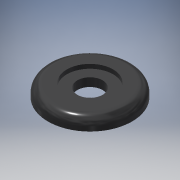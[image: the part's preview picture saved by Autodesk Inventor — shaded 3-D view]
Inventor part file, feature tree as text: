
AUTODESK INVENTOR PART (.ipt)
format: ipt  version: 2018 (Build 220112000, 112)  size: 162,816 bytes
history: native  units: mm
features: revolve x1, sketch x1
ambient origin geometry x8: Origin, YZ Plane, XZ Plane, XY Plane, X Axis, Y Axis, Z Axis, Center Point
bodies: Solid1 (feature_tree)
feature tree (2):
  revolve  "Revolution1"  [1 undecoded]
  sketch  "Sketch1"  dims[d0=5.0mm d1=4.5mm d2=3.5mm d3=1.5mm d4=1.5mm d5=0.5mm d6=0.5mm d7=2.75mm d8=1.0mm d9=0.05mm d10=90.0deg]
note: 1 required parameter value undecoded (feature->parameter linkage not recoverable at this tier; creation-order binding heuristic only, values carry confidence <= 0.55)
